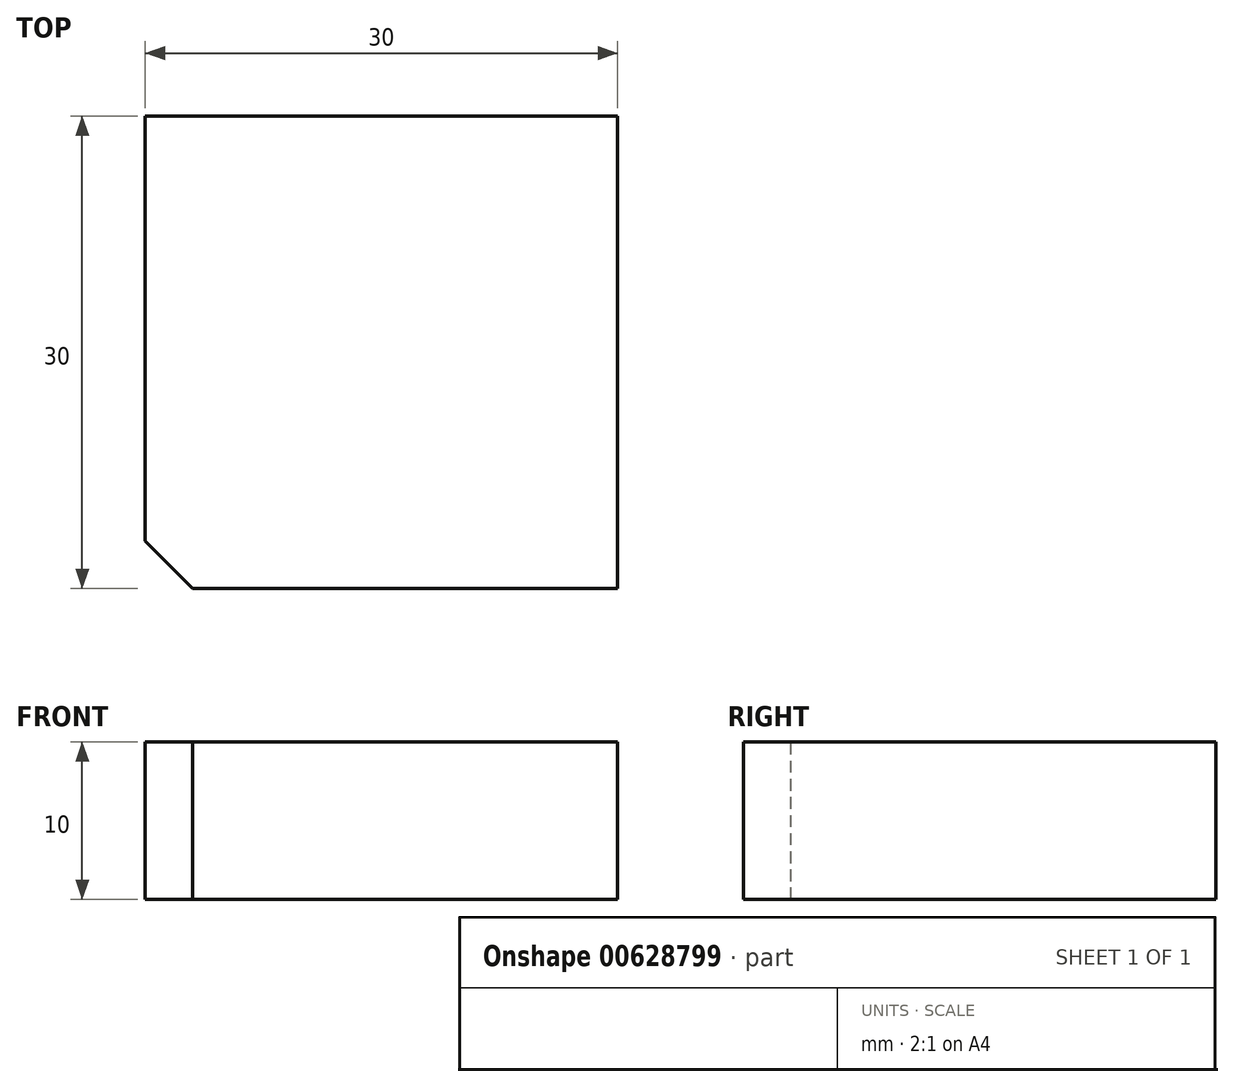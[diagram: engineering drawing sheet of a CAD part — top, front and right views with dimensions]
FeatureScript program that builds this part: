
annotation { "Feature Type Name" : "Feature", "Feature Type Description" : "" }
export const myFeature = defineFeature(function(context is Context, id is Id, definition is map)
    precondition{}
    {
        {
            var Q0;
            Q0=qCreatedBy(makeId("Top.planeOp"),FACE);
            var sketch = newSketch(context, id + "F0", { "sketchPlane" : qUnion([Q0])});
            skLineSegment(sketch, "E0.bottom", {"start": v(-15, -15) * mm, "end": v(15, -15) * mm});
            skLineSegment(sketch, "E0.top", {"start": v(-15, 15) * mm, "end": v(15, 15) * mm});
            skLineSegment(sketch, "E0.left", {"start": v(-15, -15) * mm, "end": v(-15, 15) * mm});
            skLineSegment(sketch, "E0.right", {"start": v(15, -15) * mm, "end": v(15, 15) * mm});
            skSolve(sketch);
        }
        {
            var Q0;
            Q0=makeQuery(id+"F0.imprint","IMPRINT",FACE,{"disambiguationData":[TD([[makeQuery(id+"F0.imprint","IMPRINT",EDGE,{"derivedFrom":sQuery(id+"F0.wireOp",EDGE,"E0.bottom")}),1.0]])]});
            extrude(context, id + "F1", {"entities" : qUnion([Q0]), "depth" : 10 * mm, "offsetDistance" : 25 * mm});
        }
        {
            var Q0;
            Q0=makeQuery(id+"F1.opExtrude","SWEPT_EDGE",EDGE,{"disambiguationData":[OSD([sQuery(id+"F0.wireOp",EDGE,"E0.bottom"),sQuery(id+"F0.wireOp",EDGE,"E0.left")])]});
            chamfer(context, id + "F2", {"entities" : qUnion([Q0]), "width" : 3 * mm, "tangentPropagation" : true});
        }
    });
